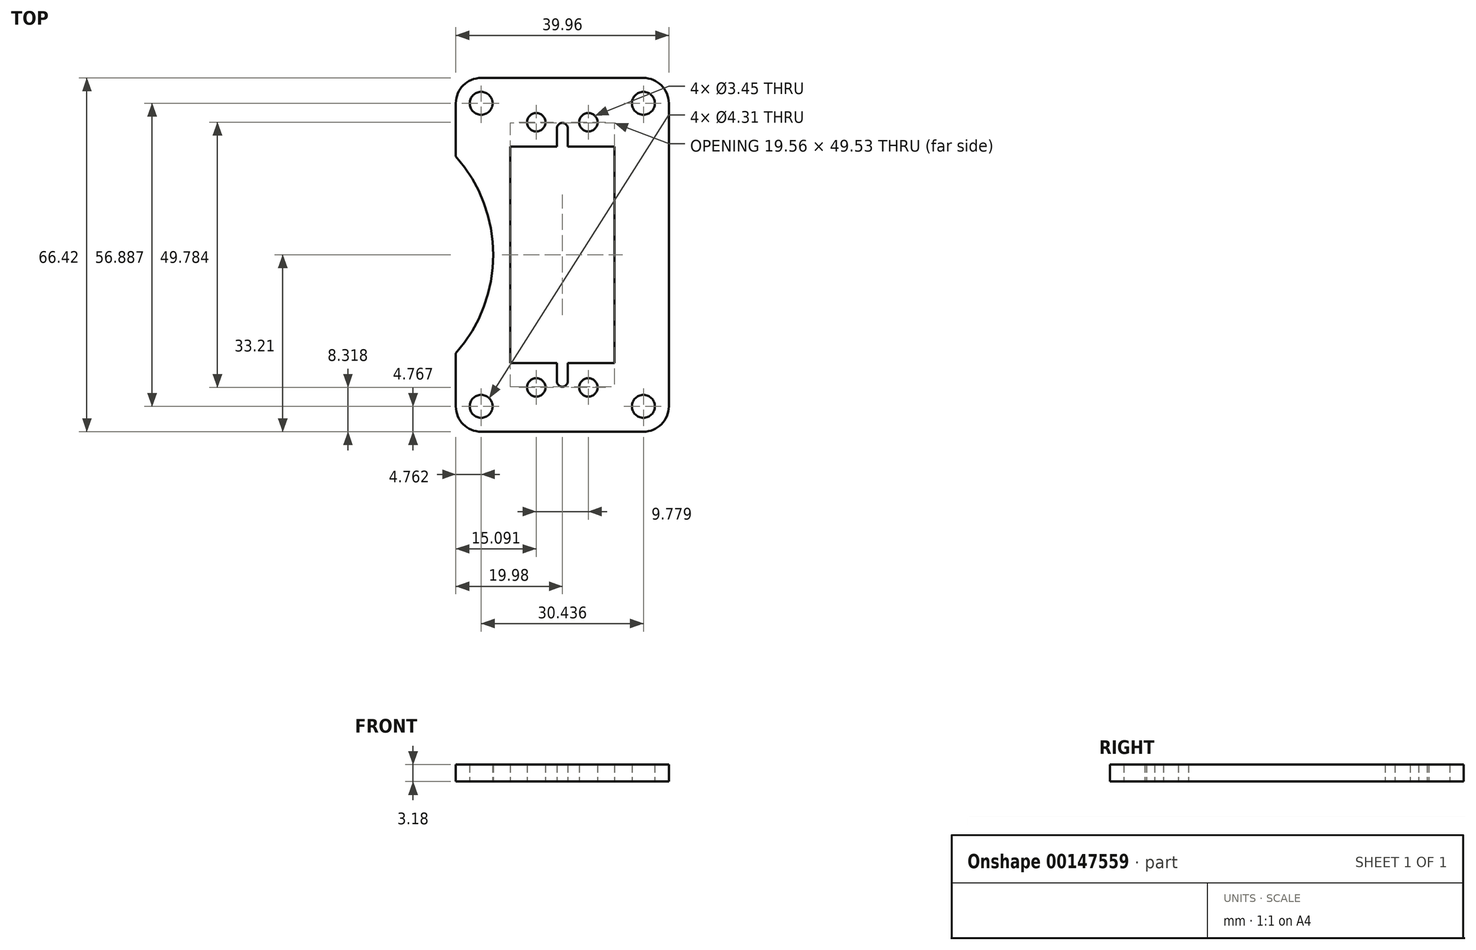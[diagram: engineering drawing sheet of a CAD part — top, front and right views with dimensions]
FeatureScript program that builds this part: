
annotation { "Feature Type Name" : "Feature", "Feature Type Description" : "" }
export const myFeature = defineFeature(function(context is Context, id is Id, definition is map)
    precondition{}
    {
        {
            var Q0;
            Q0=qCreatedBy(makeId("Top.planeOp"),FACE);
            var sketch = newSketch(context, id + "F0", { "sketchPlane" : qUnion([Q0])});
            skLineSegment(sketch, "E0.rect.bottom", {"start": v(-9.78, -20.32) * mm, "end": v(-9.78, 20.32) * mm});
            skLineSegment(sketch, "E0.rect.top", {"start": v(9.78, -20.32) * mm, "end": v(9.78, 20.32) * mm});
            skPoint(sketch, "E0.rect.middle", {"position": v(0, 0) * mm});
            skLineSegment(sketch, "E1.rect.bottom", {"start": v(-4.89, -24.9) * mm, "end": v(-4.89, 24.9) * mm, "construction": true});
            skLineSegment(sketch, "E1.rect.top", {"start": v(4.89, -24.9) * mm, "end": v(4.89, 24.9) * mm, "construction": true});
            skLineSegment(sketch, "E1.rect.left", {"start": v(-4.89, -24.9) * mm, "end": v(4.89, -24.9) * mm, "construction": true});
            skLineSegment(sketch, "E1.rect.right", {"start": v(-4.89, 24.9) * mm, "end": v(4.89, 24.9) * mm, "construction": true});
            skCircle(sketch, "E2", {"center": v(4.89, 24.9) * mm, "radius": 1.73 * mm});
            skCircle(sketch, "E3", {"center": v(-4.89, 24.9) * mm, "radius": 1.73 * mm});
            skCircle(sketch, "E4", {"center": v(4.89, -24.9) * mm, "radius": 1.73 * mm});
            skCircle(sketch, "E5", {"center": v(-4.89, -24.9) * mm, "radius": 1.73 * mm});
            skLineSegment(sketch, "E6", {"start": v(-9.78, 20.32) * mm, "end": v(-1.02, 20.32) * mm});
            skLineSegment(sketch, "E7", {"start": v(-1.02, 20.32) * mm, "end": v(-1.02, 23.75) * mm});
            skLineSegment(sketch, "E8", {"start": v(-1.02, 23.75) * mm, "end": v(1.02, 23.75) * mm, "construction": true});
            skLineSegment(sketch, "E9", {"start": v(1.02, 23.75) * mm, "end": v(1.02, 20.32) * mm});
            skLineSegment(sketch, "E10", {"start": v(1.02, 20.32) * mm, "end": v(9.78, 20.32) * mm});
            skLineSegment(sketch, "E11", {"start": v(9.78, -20.32) * mm, "end": v(1.02, -20.32) * mm});
            skLineSegment(sketch, "E12", {"start": v(1.02, -20.32) * mm, "end": v(1.02, -23.75) * mm});
            skLineSegment(sketch, "E13", {"start": v(1.02, -23.75) * mm, "end": v(-1.02, -23.75) * mm, "construction": true});
            skLineSegment(sketch, "E14", {"start": v(-1.02, -23.75) * mm, "end": v(-1.02, -20.32) * mm});
            skLineSegment(sketch, "E15", {"start": v(-1.02, -20.32) * mm, "end": v(-9.78, -20.32) * mm});
            skArc(sketch, "E16", {"start": v(1.02, 23.75) * mm, "mid": v(0, 24.77) * mm, "end": v(-1.02, 23.75) * mm});
            skArc(sketch, "E17", {"start": v(-1.02, -23.75) * mm, "mid": v(0, -24.76) * mm, "end": v(1.02, -23.75) * mm});
            skLineSegment(sketch, "E18", {"start": v(-1.02, 20.32) * mm, "end": v(1.02, 20.32) * mm, "construction": true});
            skLineSegment(sketch, "E19", {"start": v(0, 20.32) * mm, "end": v(0, 10.9) * mm, "construction": true});
            skLineSegment(sketch, "E20.bottom", {"start": v(19.98, -33.2) * mm, "end": v(-19.98, -33.2) * mm});
            skLineSegment(sketch, "E20.top", {"start": v(19.98, 33.2) * mm, "end": v(-19.98, 33.2) * mm});
            skLineSegment(sketch, "E20.left", {"start": v(19.98, -33.2) * mm, "end": v(19.98, 33.2) * mm});
            skLineSegment(sketch, "E20.right", {"start": v(-19.98, -33.2) * mm, "end": v(-19.98, 33.2) * mm});
            skLineSegment(sketch, "E21", {"start": v(0, -24.9) * mm, "end": v(0, -33.2) * mm, "construction": true});
            skLineSegment(sketch, "E22", {"start": v(-15.22, 33.2) * mm, "end": v(-15.22, 28.44) * mm, "construction": true});
            skLineSegment(sketch, "E23", {"start": v(-15.22, 28.44) * mm, "end": v(-19.98, 28.44) * mm, "construction": true});
            skLineSegment(sketch, "E24", {"start": v(0, 0) * mm, "end": v(0, 0) * mm});
            skLineSegment(sketch, "E25.bottom", {"start": v(-15.22, 28.44) * mm, "end": v(15.22, 28.44) * mm, "construction": true});
            skLineSegment(sketch, "E25.top", {"start": v(-15.22, -28.44) * mm, "end": v(15.22, -28.44) * mm, "construction": true});
            skLineSegment(sketch, "E25.left", {"start": v(-15.22, 28.44) * mm, "end": v(-15.22, -28.44) * mm, "construction": true});
            skLineSegment(sketch, "E25.right", {"start": v(15.22, 28.44) * mm, "end": v(15.22, -28.44) * mm, "construction": true});
            skLineSegment(sketch, "E26", {"start": v(0, 24.9) * mm, "end": v(0, 33.2) * mm, "construction": true});
            skLineSegment(sketch, "E27", {"start": v(0, 0) * mm, "end": v(-40.74, 0) * mm, "construction": true});
            skLineSegment(sketch, "E28", {"start": v(0, 10.9) * mm, "end": v(-40.74, 0) * mm, "construction": true});
            skCircle(sketch, "E29", {"center": v(-40.74, 0) * mm, "radius": 25.3 * mm, "construction": true});
            skCircle(sketch, "E30", {"center": v(-15.22, 28.44) * mm, "radius": 2.15 * mm});
            skCircle(sketch, "E31", {"center": v(15.22, 28.44) * mm, "radius": 2.15 * mm});
            skCircle(sketch, "E32", {"center": v(-15.22, -28.44) * mm, "radius": 2.15 * mm});
            skCircle(sketch, "E33", {"center": v(15.22, -28.44) * mm, "radius": 2.15 * mm});
            skCircle(sketch, "E34", {"center": v(-4.89, 24.9) * mm, "radius": 4.57 * mm, "construction": true});
            skCircle(sketch, "E35", {"center": v(0, 10.9) * mm, "radius": 16.88 * mm, "construction": true});
            skCircle(sketch, "E36", {"center": v(-15.22, 28.44) * mm, "radius": 6.35 * mm, "construction": true});
            skSolve(sketch);
        }
        {
            var Q0;
            Q0=qSketchRegion(id+"F0",true);
            extrude(context, id + "F1", {"entities" : qUnion([Q0]), "depth" : 3.17 * mm});
        }
        {
            var Q0;
            Q0=makeQuery(id+"F1.opExtrude","SWEPT_EDGE",EDGE,{"disambiguationData":[OSD([sQuery(id+"F0.wireOp",EDGE,"E20.top"),sQuery(id+"F0.wireOp",EDGE,"E20.left")])]});
            var Q1;
            Q1=makeQuery(id+"F1.opExtrude","SWEPT_EDGE",EDGE,{"disambiguationData":[OSD([sQuery(id+"F0.wireOp",EDGE,"E20.bottom"),sQuery(id+"F0.wireOp",EDGE,"E20.left")])]});
            var Q2;
            Q2=makeQuery(id+"F1.opExtrude","SWEPT_EDGE",EDGE,{"disambiguationData":[OSD([sQuery(id+"F0.wireOp",EDGE,"E20.top"),sQuery(id+"F0.wireOp",EDGE,"E20.right")])]});
            var Q3;
            Q3=makeQuery(id+"F1.opExtrude","SWEPT_EDGE",EDGE,{"disambiguationData":[OSD([sQuery(id+"F0.wireOp",EDGE,"E20.bottom"),sQuery(id+"F0.wireOp",EDGE,"E20.right")])]});
            fillet(context, id + "F2", {"entities" : qUnion([Q0, Q1, Q2, Q3]), "radius" : 4.76 * mm, "tangentPropagation" : true, "allowEdgeOverflow" : false});
        }
        {
            var Q0;
            Q0=makeQuery(id+"F1.opExtrude","CAP_FACE",FACE,{"disambiguationData":[OSD([sQuery(id+"F0.wireOp",EDGE,"E0.rect.bottom"),sQuery(id+"F0.wireOp",EDGE,"E0.rect.top"),sQuery(id+"F0.wireOp",EDGE,"E2"),sQuery(id+"F0.wireOp",EDGE,"E3"),sQuery(id+"F0.wireOp",EDGE,"E4"),sQuery(id+"F0.wireOp",EDGE,"E5"),sQuery(id+"F0.wireOp",EDGE,"E6"),sQuery(id+"F0.wireOp",EDGE,"E7"),sQuery(id+"F0.wireOp",EDGE,"E9"),sQuery(id+"F0.wireOp",EDGE,"E10"),sQuery(id+"F0.wireOp",EDGE,"E11"),sQuery(id+"F0.wireOp",EDGE,"E12"),sQuery(id+"F0.wireOp",EDGE,"E14"),sQuery(id+"F0.wireOp",EDGE,"E15"),sQuery(id+"F0.wireOp",EDGE,"E16"),sQuery(id+"F0.wireOp",EDGE,"E17"),sQuery(id+"F0.wireOp",EDGE,"E20.bottom"),sQuery(id+"F0.wireOp",EDGE,"E20.top"),sQuery(id+"F0.wireOp",EDGE,"E20.left"),sQuery(id+"F0.wireOp",EDGE,"E20.right"),sQuery(id+"F0.wireOp",EDGE,"E30"),sQuery(id+"F0.wireOp",EDGE,"E31"),sQuery(id+"F0.wireOp",EDGE,"E32"),sQuery(id+"F0.wireOp",EDGE,"E33")])],"isStart":true});
            var sketch = newSketch(context, id + "F3", { "sketchPlane" : qUnion([Q0])});
            skLineSegment(sketch, "E37", {"start": v(-9.78, 0) * mm, "end": v(-12.95, 0) * mm, "construction": true});
            skLineSegment(sketch, "E38", {"start": v(-12.95, 0) * mm, "end": v(-40.74, 0) * mm, "construction": true});
            skArc(sketch, "E39", {"start": v(-19.98, -18.47) * mm, "mid": v(-12.95, 0) * mm, "end": v(-19.98, 18.47) * mm});
            skLineSegment(sketch, "E40", {"start": v(-19.98, 18.47) * mm, "end": v(-19.98, -18.47) * mm});
            skSolve(sketch);
        }
        {
            var Q0;
            Q0=qSketchRegion(id+"F3",true);
            var Q1;
            Q1=makeQuery(id+"F1.opExtrude","CAP_FACE",FACE,{"disambiguationData":[OSD([sQuery(id+"F0.wireOp",EDGE,"E0.rect.bottom"),sQuery(id+"F0.wireOp",EDGE,"E0.rect.top"),sQuery(id+"F0.wireOp",EDGE,"E2"),sQuery(id+"F0.wireOp",EDGE,"E3"),sQuery(id+"F0.wireOp",EDGE,"E4"),sQuery(id+"F0.wireOp",EDGE,"E5"),sQuery(id+"F0.wireOp",EDGE,"E6"),sQuery(id+"F0.wireOp",EDGE,"E7"),sQuery(id+"F0.wireOp",EDGE,"E9"),sQuery(id+"F0.wireOp",EDGE,"E10"),sQuery(id+"F0.wireOp",EDGE,"E11"),sQuery(id+"F0.wireOp",EDGE,"E12"),sQuery(id+"F0.wireOp",EDGE,"E14"),sQuery(id+"F0.wireOp",EDGE,"E15"),sQuery(id+"F0.wireOp",EDGE,"E16"),sQuery(id+"F0.wireOp",EDGE,"E17"),sQuery(id+"F0.wireOp",EDGE,"E20.bottom"),sQuery(id+"F0.wireOp",EDGE,"E20.top"),sQuery(id+"F0.wireOp",EDGE,"E20.left"),sQuery(id+"F0.wireOp",EDGE,"E20.right"),sQuery(id+"F0.wireOp",EDGE,"E30"),sQuery(id+"F0.wireOp",EDGE,"E31"),sQuery(id+"F0.wireOp",EDGE,"E32"),sQuery(id+"F0.wireOp",EDGE,"E33")])],"isStart":false});
            extrude(context, id + "F4", {"entities" : qUnion([Q0]), "operationType" : NewBodyOperationType.REMOVE, "endBound" : BoundingType.UP_TO_SURFACE, "oppositeDirection" : true, "endBoundEntityFace" : qUnion([Q1]), "depth" : 25.4 * mm});
        }
    });
